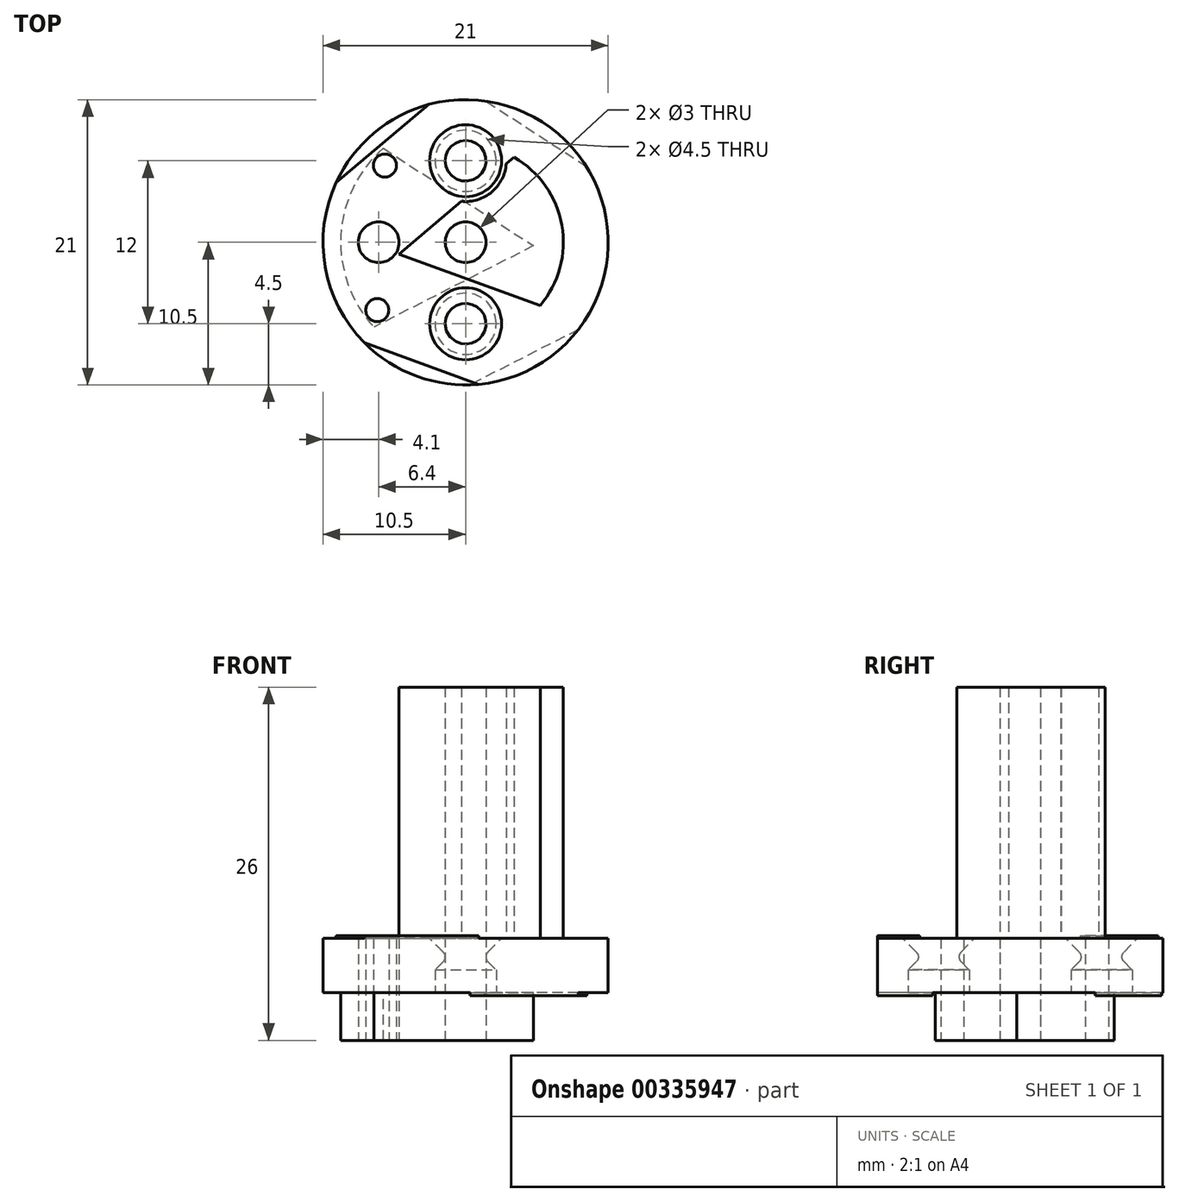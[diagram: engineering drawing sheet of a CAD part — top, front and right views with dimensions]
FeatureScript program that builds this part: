
annotation { "Feature Type Name" : "Feature", "Feature Type Description" : "" }
export const myFeature = defineFeature(function(context is Context, id is Id, definition is map)
    precondition{}
    {
        {
            var Q0;
            Q0=qCreatedBy(makeId("Top.planeOp"),FACE);
            var sketch = newSketch(context, id + "F0", { "sketchPlane" : qUnion([Q0])});
            skCircle(sketch, "E0", {"center": v(0, 0) * mm, "radius": 10.5 * mm});
            skCircle(sketch, "E1", {"center": v(0, 0) * mm, "radius": 1.5 * mm});
            skCircle(sketch, "E2", {"center": v(0, 6) * mm, "radius": 1.5 * mm});
            skCircle(sketch, "E3", {"center": v(0, -6) * mm, "radius": 1.5 * mm});
            skCircle(sketch, "E4", {"center": v(-6.4, 0) * mm, "radius": 1.5 * mm});
            skLineSegment(sketch, "E5", {"start": v(0, 6) * mm, "end": v(0, 0) * mm, "construction": true});
            skLineSegment(sketch, "E6", {"start": v(0, 0) * mm, "end": v(0, -6) * mm, "construction": true});
            skLineSegment(sketch, "E7", {"start": v(0, 0) * mm, "end": v(-6.4, 0) * mm, "construction": true});
            skSolve(sketch);
        }
        {
            var Q0;
            Q0 = qSketchRegion(id + "F0", true);
            extrude(context, id + "F1", {"entities" : qUnion([Q0]), "depth" : 4 * mm});
        }
        {
            var Q0;
            Q0=qCreatedBy(makeId("Right.planeOp"),FACE);
            var sketch = newSketch(context, id + "F2", { "sketchPlane" : qUnion([Q0])});
            skLineSegment(sketch, "E8.0", {"start": v(-7.5, 4) * mm, "end": v(-4.5, 4) * mm, "construction": true});
            skLineSegment(sketch, "E9.0", {"start": v(-7.5, 0) * mm, "end": v(-4.5, 0) * mm, "construction": true});
            skLineSegment(sketch, "E10", {"start": v(-7.5, 4) * mm, "end": v(-7.5, 0) * mm, "construction": true});
            skLineSegment(sketch, "E11", {"start": v(-4.5, 0) * mm, "end": v(-4.5, 4) * mm, "construction": true});
            skLineSegment(sketch, "E12", {"start": v(-6, 4) * mm, "end": v(-6, 0) * mm, "construction": true});
            skLineSegment(sketch, "E13", {"start": v(-7.65, 3) * mm, "end": v(-8.65, 4) * mm});
            skLineSegment(sketch, "E14", {"start": v(-8.25, 0) * mm, "end": v(-8.25, 1.69) * mm});
            skLineSegment(sketch, "E15", {"start": v(-8.25, 1.69) * mm, "end": v(-7.65, 2.29) * mm});
            skLineSegment(sketch, "E16", {"start": v(-8.65, 4) * mm, "end": v(-7.5, 4) * mm});
            skLineSegment(sketch, "E17", {"start": v(-8.25, 0) * mm, "end": v(-7.5, 0) * mm});
            skPoint(sketch, "E18.visualSharp", {"position": v(-7.3, 2.64) * mm});
            skArc(sketch, "E18.filletArc", {"start": v(-7.65, 2.29) * mm, "mid": v(-7.5, 2.64) * mm, "end": v(-7.65, 3) * mm});
            skLineSegment(sketch, "E19", {"start": v(-7.5, 4) * mm, "end": v(-7.5, 0) * mm});
            skPoint(sketch, "E20", {"position": v(-7.5, 2.64) * mm});
            skLineSegment(sketch, "E21.MirrorCS", {"start": v(6, 4) * mm, "end": v(6, 0) * mm, "construction": true});
            skLineSegment(sketch, "E22.MirrorCS", {"start": v(8.65, 4) * mm, "end": v(7.5, 4) * mm});
            skLineSegment(sketch, "E23.MirrorCS", {"start": v(7.65, 3) * mm, "end": v(8.65, 4) * mm});
            skArc(sketch, "E24.MirrorCS", {"start": v(7.65, 2.29) * mm, "mid": v(7.5, 2.64) * mm, "end": v(7.65, 3) * mm});
            skLineSegment(sketch, "E25.MirrorCS", {"start": v(7.5, 4) * mm, "end": v(7.5, 0) * mm});
            skLineSegment(sketch, "E26.MirrorCS", {"start": v(8.25, 1.69) * mm, "end": v(7.65, 2.29) * mm});
            skLineSegment(sketch, "E27.MirrorCS", {"start": v(8.25, 0) * mm, "end": v(8.25, 1.69) * mm});
            skLineSegment(sketch, "E28.MirrorCS", {"start": v(8.25, 0) * mm, "end": v(7.5, 0) * mm});
            skSolve(sketch);
        }
        {
            var Q0;
            Q0=makeQuery(id+"F2.imprint","IMPRINT",FACE,{"disambiguationData":[TD([[makeQuery(id+"F2.imprint","IMPRINT",EDGE,{"derivedFrom":sQuery(id+"F2.wireOp",EDGE,"E14")}),-1.0]])]});
            var Q1;
            {var subQ0=sQuery(id+"F2.wireOp",EDGE,"E13");Q1=makeQuery(id+"F2.imprint","IMPRINT",FACE,{"disambiguationData":[TD([[makeQuery(id+"F2.imprint","IMPRINT",EDGE,{"derivedFrom":subQ0}),-1.0]])]});}
            var Q2;
            Q2=sQuery(id+"F2.wireOp",EDGE,"E12");
            revolve(context, id + "F3", {"operationType" : NewBodyOperationType.REMOVE, "entities" : qUnion([Q0, Q1]), "axis" : qUnion([Q2]), "revolveType" : RevolveType.FULL, "oppositeDirection" : true});
        }
        {
            var Q0;
            {var subQ0=sQuery(id+"F2.wireOp",EDGE,"E22.MirrorCS");Q0=makeQuery(id+"F2.imprint","IMPRINT",FACE,{"disambiguationData":[TD([[makeQuery(id+"F2.imprint","IMPRINT",EDGE,{"derivedFrom":subQ0}),1.0]])]});}
            var Q1;
            {var subQ0=sQuery(id+"F2.wireOp",EDGE,"E26.MirrorCS");Q1=makeQuery(id+"F2.imprint","IMPRINT",FACE,{"disambiguationData":[TD([[makeQuery(id+"F2.imprint","IMPRINT",EDGE,{"derivedFrom":subQ0}),1.0]])]});}
            var Q2;
            Q2=sQuery(id+"F2.wireOp",EDGE,"E21.MirrorCS");
            revolve(context, id + "F4", {"operationType" : NewBodyOperationType.REMOVE, "entities" : qUnion([Q0, Q1]), "axis" : qUnion([Q2]), "revolveType" : RevolveType.FULL, "oppositeDirection" : true});
        }
        {
            var Q0;
            Q0=makeQuery(id+"F1.opExtrude","CAP_FACE",FACE,{"disambiguationData":[OSD([sQuery(id+"F0.wireOp",EDGE,"E0"),sQuery(id+"F0.wireOp",EDGE,"E1"),sQuery(id+"F0.wireOp",EDGE,"E2"),sQuery(id+"F0.wireOp",EDGE,"E3"),sQuery(id+"F0.wireOp",EDGE,"E4")])],"isStart":false});
            var sketch = newSketch(context, id + "F5", { "sketchPlane" : qUnion([Q0])});
            skCircle(sketch, "E29.0", {"center": v(0, 0) * mm, "radius": 10.5 * mm, "construction": true});
            skLineSegment(sketch, "E30", {"start": v(6.2, 8.47) * mm, "end": v(-4.92, -0.87) * mm});
            skLineSegment(sketch, "E31", {"start": v(-4.92, -0.87) * mm, "end": v(8.73, -5.84) * mm});
            skCircle(sketch, "E32", {"center": v(0, 0) * mm, "radius": 2.5 * mm, "construction": true});
            skArc(sketch, "E33", {"start": v(-0.3, 3.01) * mm, "mid": v(1.93, 3.7) * mm, "end": v(3, 5.77) * mm});
            skArc(sketch, "E34", {"start": v(3.57, 6.26) * mm, "mid": v(7.1, 1.25) * mm, "end": v(5.49, -4.66) * mm});
            skArc(sketch, "E35", {"start": v(5.18, 7.6) * mm, "mid": v(9.06, 1.6) * mm, "end": v(7.46, -5.38) * mm});
            skCircle(sketch, "E36.0", {"center": v(0, 0) * mm, "radius": 1.5 * mm});
            skLineSegment(sketch, "E37", {"start": v(-9.53, 4.4) * mm, "end": v(-2.68, 10.15) * mm});
            skLineSegment(sketch, "E38", {"start": v(-7.45, -7.4) * mm, "end": v(0.95, -10.46) * mm});
            skArc(sketch, "E39", {"start": v(-9.53, 4.4) * mm, "mid": v(-6.75, 8.04) * mm, "end": v(-2.68, 10.15) * mm});
            skArc(sketch, "E40", {"start": v(0.95, -10.46) * mm, "mid": v(-3.6, -9.87) * mm, "end": v(-7.45, -7.4) * mm});
            skSolve(sketch);
        }
        {
            var Q0;
            Q0=makeQuery(id+"F5.imprint","IMPRINT",FACE,{"disambiguationData":[TD([[makeQuery(id+"F5.imprint","IMPRINT",EDGE,{"derivedFrom":sQuery(id+"F5.wireOp",EDGE,"E37")}),1.0]])]});
            var Q1;
            Q1=makeQuery(id+"F5.imprint","IMPRINT",FACE,{"disambiguationData":[TD([[makeQuery(id+"F5.imprint","IMPRINT",EDGE,{"derivedFrom":sQuery(id+"F5.wireOp",EDGE,"E38")}),-1.0]])]});
            extrude(context, id + "F6", {"entities" : qUnion([Q0, Q1]), "operationType" : NewBodyOperationType.ADD, "depth" : 0.2 * mm});
        }
        {
            var Q0;
            {var subQ0=sQuery(id+"F5.wireOp",EDGE,"E33");Q0=makeQuery(id+"F5.imprint","IMPRINT",FACE,{"disambiguationData":[TD([[makeQuery(id+"F5.imprint","IMPRINT",EDGE,{"derivedFrom":subQ0}),-1.0]])]});}
            extrude(context, id + "F7", {"entities" : qUnion([Q0]), "operationType" : NewBodyOperationType.ADD, "depth" : 9.8 * mm});
        }
        {
            var Q0;
            {var subQ0=sQuery(id+"F5.wireOp",EDGE,"E34");Q0=makeQuery(id+"F5.imprint","IMPRINT",FACE,{"disambiguationData":[TD([[makeQuery(id+"F5.imprint","IMPRINT",EDGE,{"derivedFrom":subQ0}),1.0]])]});}
            extrude(context, id + "F8", {"entities" : qUnion([Q0]), "operationType" : NewBodyOperationType.ADD, "depth" : 18.5 * mm});
        }
        {
            var Q0;
            Q0=makeQuery(id+"F8.opExtrude","CAP_FACE",FACE,{"disambiguationData":[OSD([sQuery(id+"F5.wireOp",EDGE,"E30"),sQuery(id+"F5.wireOp",EDGE,"E31"),sQuery(id+"F5.wireOp",EDGE,"E34"),sQuery(id+"F5.wireOp",EDGE,"E35")])],"isStart":false});
            var sketch = newSketch(context, id + "F9", { "sketchPlane" : qUnion([Q0])});
            skArc(sketch, "E41", {"start": v(4.38, 6.94) * mm, "mid": v(8.08, 1.42) * mm, "end": v(6.48, -5.02) * mm, "construction": true});
            skCircle(sketch, "E42", {"center": v(5.21, 6.33) * mm, "radius": 0.7 * mm});
            skCircle(sketch, "E43", {"center": v(8.08, 1.42) * mm, "radius": 0.7 * mm});
            skCircle(sketch, "E44", {"center": v(7.4, -3.54) * mm, "radius": 0.7 * mm});
            skLineSegment(sketch, "E45", {"start": v(0, 0) * mm, "end": v(8.08, 1.42) * mm, "construction": true});
            skSolve(sketch);
        }
        {
            var Q0;
            Q0 = qSketchRegion(id + "F9", true);
            extrude(context, id + "F10", {"entities" : qUnion([Q0]), "operationType" : NewBodyOperationType.REMOVE, "oppositeDirection" : true, "depth" : 8 * mm});
        }
        {
            var Q0;
            Q0=makeQuery(id+"F1.opExtrude","CAP_FACE",FACE,{"disambiguationData":[OSD([sQuery(id+"F0.wireOp",EDGE,"E0"),sQuery(id+"F0.wireOp",EDGE,"E1"),sQuery(id+"F0.wireOp",EDGE,"E2"),sQuery(id+"F0.wireOp",EDGE,"E3"),sQuery(id+"F0.wireOp",EDGE,"E4")])],"isStart":true});
            var sketch = newSketch(context, id + "F11", { "sketchPlane" : qUnion([Q0])});
            skCircle(sketch, "E46.0", {"center": v(0, 0) * mm, "radius": 10.5 * mm, "construction": true});
            skLineSegment(sketch, "E47", {"start": v(-7.2, -7.65) * mm, "end": v(5, 0.26) * mm});
            skLineSegment(sketch, "E48", {"start": v(5, 0.26) * mm, "end": v(-7.95, 6.86) * mm});
            skCircle(sketch, "E49", {"center": v(0, 0) * mm, "radius": 2.5 * mm, "construction": true});
            skCircle(sketch, "E50.0", {"center": v(0, 0) * mm, "radius": 1.5 * mm});
            skCircle(sketch, "E51.0", {"center": v(-6.4, 0) * mm, "radius": 1.5 * mm});
            skArc(sketch, "E52", {"start": v(-6.06, -6.92) * mm, "mid": v(-9.19, -0.48) * mm, "end": v(-6.75, 6.25) * mm});
            skLineSegment(sketch, "E53", {"start": v(8.92, -5.53) * mm, "end": v(1.42, -10.4) * mm});
            skLineSegment(sketch, "E54", {"start": v(8.3, 6.43) * mm, "end": v(0.33, 10.5) * mm});
            skArc(sketch, "E55", {"start": v(8.92, -5.53) * mm, "mid": v(5.72, -8.8) * mm, "end": v(1.42, -10.4) * mm});
            skArc(sketch, "E56", {"start": v(0.33, 10.5) * mm, "mid": v(4.77, 9.36) * mm, "end": v(8.3, 6.43) * mm});
            skSolve(sketch);
        }
        {
            var Q0;
            Q0=makeQuery(id+"F11.imprint","IMPRINT",FACE,{"disambiguationData":[TD([[makeQuery(id+"F11.imprint","IMPRINT",EDGE,{"derivedFrom":sQuery(id+"F11.wireOp",EDGE,"E50.0")}),1.0]])]});
            extrude(context, id + "F12", {"entities" : qUnion([Q0]), "operationType" : NewBodyOperationType.ADD, "depth" : 3.5 * mm});
        }
        {
            var Q0;
            Q0=makeQuery(id+"F12.opExtrude","CAP_FACE",FACE,{"disambiguationData":[OSD([sQuery(id+"F11.wireOp",EDGE,"E47"),sQuery(id+"F11.wireOp",EDGE,"E48"),sQuery(id+"F11.wireOp",EDGE,"E50.0"),sQuery(id+"F11.wireOp",EDGE,"E51.0"),sQuery(id+"F11.wireOp",EDGE,"E52")])],"isStart":false});
            var sketch = newSketch(context, id + "F13", { "sketchPlane" : qUnion([Q0])});
            skArc(sketch, "E57", {"start": v(-5.19, -6.35) * mm, "mid": v(-8.19, -0.43) * mm, "end": v(-5.82, 5.77) * mm, "construction": true});
            skCircle(sketch, "E58", {"center": v(-5.94, -5.65) * mm, "radius": 0.85 * mm});
            skCircle(sketch, "E59", {"center": v(-6.5, 5) * mm, "radius": 0.85 * mm});
            skSolve(sketch);
        }
        {
            var Q0;
            Q0 = qSketchRegion(id + "F13", true);
            extrude(context, id + "F14", {"entities" : qUnion([Q0]), "operationType" : NewBodyOperationType.REMOVE, "endBound" : BoundingType.THROUGH_ALL, "oppositeDirection" : true, "depth" : 25 * mm});
        }
        {
            var Q0;
            Q0=makeQuery(id+"F11.imprint","IMPRINT",FACE,{"disambiguationData":[TD([[makeQuery(id+"F11.imprint","IMPRINT",EDGE,{"derivedFrom":sQuery(id+"F11.wireOp",EDGE,"E53")}),1.0]])]});
            var Q1;
            Q1=makeQuery(id+"F11.imprint","IMPRINT",FACE,{"disambiguationData":[TD([[makeQuery(id+"F11.imprint","IMPRINT",EDGE,{"derivedFrom":sQuery(id+"F11.wireOp",EDGE,"E54")}),-1.0]])]});
            extrude(context, id + "F15", {"entities" : qUnion([Q0, Q1]), "operationType" : NewBodyOperationType.ADD, "depth" : 0.2 * mm});
        }
    });
